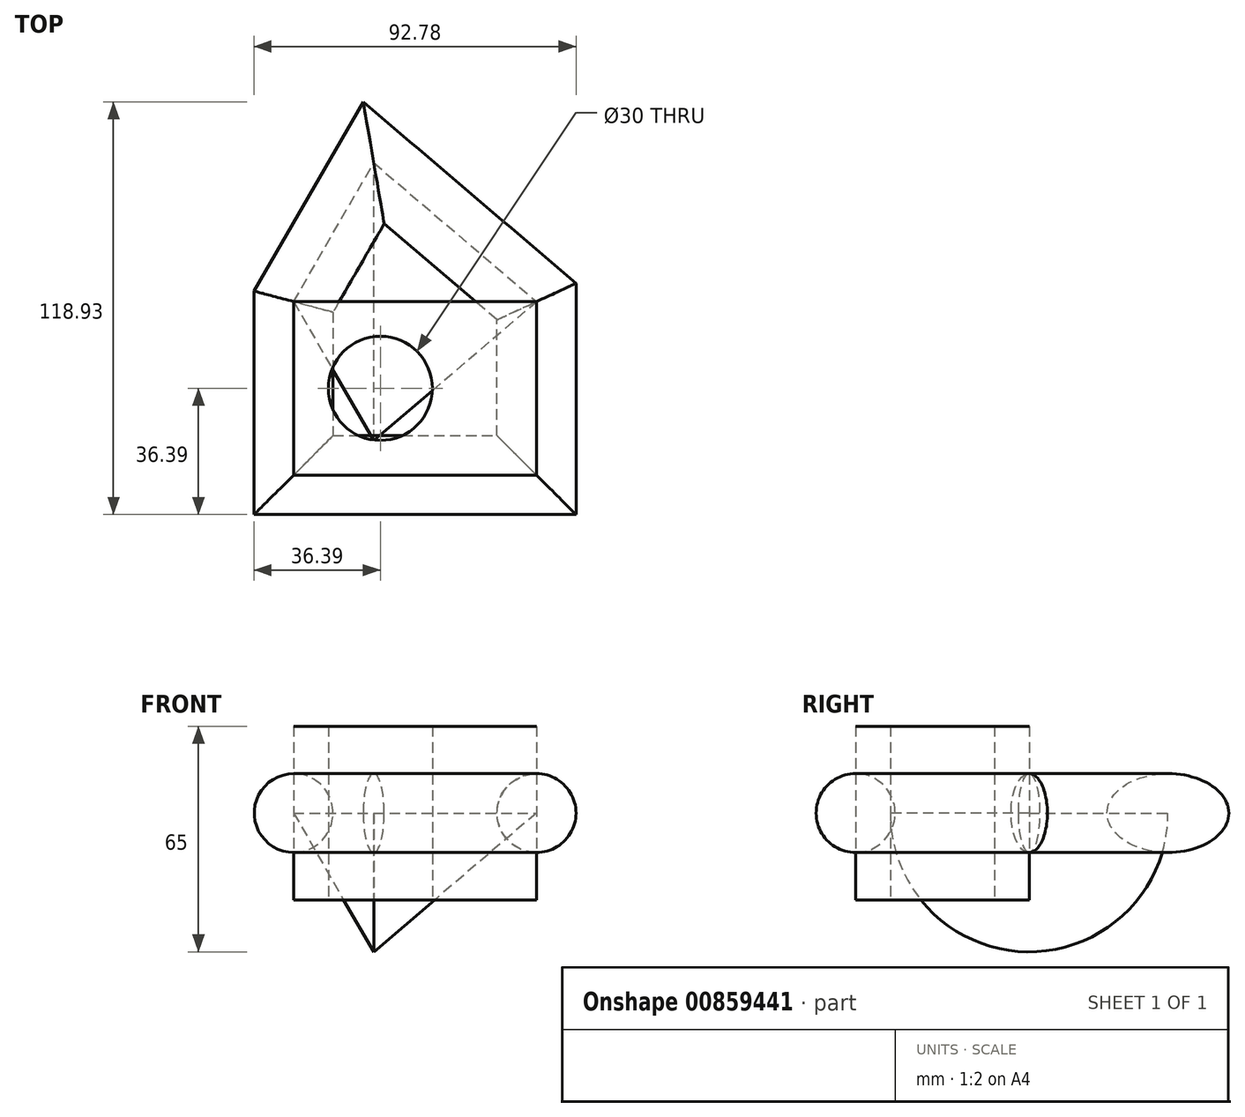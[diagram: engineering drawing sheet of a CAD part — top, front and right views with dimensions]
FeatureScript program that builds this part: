
annotation { "Feature Type Name" : "Feature", "Feature Type Description" : "" }
export const myFeature = defineFeature(function(context is Context, id is Id, definition is map)
    precondition{}
    {
        {
            var Q0;
            Q0=qCreatedBy(makeId("Top.planeOp"),FACE);
            var sketch = newSketch(context, id + "F0", { "sketchPlane" : qUnion([Q0])});
            skLineSegment(sketch, "E0.bottom", {"start": v(-35, 50) * mm, "end": v(35, 50) * mm});
            skLineSegment(sketch, "E0.top", {"start": v(-35, 0) * mm, "end": v(35, 0) * mm});
            skLineSegment(sketch, "E0.left", {"start": v(-35, 50) * mm, "end": v(-35, 0) * mm});
            skLineSegment(sketch, "E0.right", {"start": v(35, 50) * mm, "end": v(35, 0) * mm});
            skCircle(sketch, "E1", {"center": v(-10, 25) * mm, "radius": 15 * mm});
            skLineSegment(sketch, "E2", {"start": v(-35, 50) * mm, "end": v(-11.9, 90) * mm});
            skLineSegment(sketch, "E3", {"start": v(-11.9, 90) * mm, "end": v(35, 50) * mm});
            skSolve(sketch);
        }
        {
            var Q0;
            Q0=makeQuery(id+"F0.imprint","IMPRINT",FACE,{"disambiguationData":[TD([[makeQuery(id+"F0.imprint","IMPRINT",EDGE,{"derivedFrom":sQuery(id+"F0.wireOp",EDGE,"E0.bottom")}),-1.0]])]});
            extrude(context, id + "F1", {"entities" : qUnion([Q0]), "endBound" : BoundingType.SYMMETRIC, "depth" : 50 * mm, "offsetDistance" : 25 * mm});
        }
        {
            var Q0;
            Q0=makeQuery(id+"F0.imprint","IMPRINT",FACE,{"disambiguationData":[TD([[makeQuery(id+"F0.imprint","IMPRINT",EDGE,{"derivedFrom":sQuery(id+"F0.wireOp",EDGE,"E0.bottom")}),1.0]])]});
            var Q1;
            Q1=sQuery(id+"F0.wireOp",EDGE,"E0.bottom");
            revolve(context, id + "F2", {"surfaceOperationType" : NewSurfaceOperationType.NEW, "entities" : qUnion([Q0]), "axis" : qUnion([Q1]), "revolveType" : RevolveType.ONE_DIRECTION, "oppositeDirection" : true, "angle" : 180 * degree});
        }
        {
            var Q0;
            Q0=qCreatedBy(makeId("Right.planeOp"),FACE);
            var Q1;
            Q1=sQuery(id+"F0.wireOp",VERTEX,"E0.top.start");
            cPlane(context, id + "F3", {"entities" : qUnion([Q0, Q1]), "cplaneType" : CPlaneType.PLANE_POINT, "offset" : 25 * mm, "width" : 150 * mm, "height" : 150 * mm});
        }
        {
            var Q0;
            Q0=qCreatedBy(id+"F3.planeOp",FACE);
            var sketch = newSketch(context, id + "F4", { "sketchPlane" : qUnion([Q0])});
            skCircle(sketch, "E4", {"center": v(0, 0) * mm, "radius": 11.39 * mm});
            skSolve(sketch);
        }
        {
            var Q0;
            Q0=makeQuery(id+"F4.imprint","IMPRINT",FACE,{"disambiguationData":[TD([[makeQuery(id+"F4.imprint","IMPRINT",EDGE,{"derivedFrom":sQuery(id+"F4.wireOp",EDGE,"E4")}),1.0]])]});
            var Q1;
            Q1=sQuery(id+"F0.wireOp",EDGE,"E0.top");
            var Q2;
            Q2=sQuery(id+"F0.wireOp",EDGE,"E0.right");
            var Q3;
            Q3=sQuery(id+"F0.wireOp",EDGE,"E3");
            var Q4;
            Q4=sQuery(id+"F0.wireOp",EDGE,"E2");
            var Q5;
            Q5=sQuery(id+"F0.wireOp",EDGE,"E0.left");
            sweep(context, id + "F5", {"profiles" : qUnion([Q0]), "path" : qUnion([Q1, Q2, Q3, Q4, Q5])});
        }
    });
